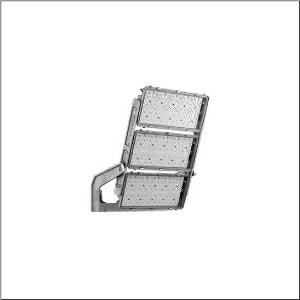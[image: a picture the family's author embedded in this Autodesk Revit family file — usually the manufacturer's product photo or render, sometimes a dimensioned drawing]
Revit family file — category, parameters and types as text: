
# Revit family: floodlight_fl_11_maxi_pro_remote___pl43_5xa779528a01aa_9860
name_source: partatom
category: Lighting Fixtures
units: mm (PartAtom-declared; Revit-internal decimal feet)

## family parameters
Cut with Voids When Loaded = No
Host = Face
Light Source = No
Part Type = Normal
Room Calculation Point = No
Round Connector Dimension = Use Diameter
Shared = No

## types (1)
- --- (1 x LED, 156040 lm, 1388 W, 5700K)
    Apparent Load = 1388 VA
    CIE Flux Codes = 25 74 99 100 100
    Color Rendering = 80
    Color Temperature = 5700K
    Default Elevation = 1800 mm
    Description = Floodlight FL 11  maxi  pro Remote floodlight; light control with lens of PMMA; cover panel of toughened safety glass, transparent; light distribution: PL43, asymmetric direct distribution, LEDcolour temperature: 5700K, colour rendering: CRI > 80, light colour: 857; brightness control: DMX+RDM; with terminal, 8-pole, max. 2.5mm², mains connection: 220..240V/380..400V AC, 50/60Hz, surge voltage resistance: line to ground: 10kV, ECG replaceable separately, LED unit replaceable without ESD environment, dustproof LED module, LED unit replaceable, LED unit replaceable on mast without ESD environment, dimming range 10..100%; floodlight with 3x LED unit of diecast aluminium, coated grey; length: 1.003mm / width: 651mm / height: 338mm; mounting bracket, of diecast aluminium, uncoated, natural, equipment: Power, protection rating (complete): IP66; insulation class (complete): insulation class I (protective earthing); certification: CE, ENEC, VDE; ball protection: ball impact resistance with accessories, only for outdoor installations, rated ambient temperature 10°C, permissible operating ambient temperature: -40..+30°C, permissible storage temperature: -40..+85°C; packaging unit: 1 piece

Light Distribution: PL43
    Height = 320 mm
    Lamp = 1 x LED
    Lamp Light Flux = 156040 lm
    Lamp Power = 1388 W
    Lamp count = 1
    Length = 1002 mm
    Luminous efficacy = 112 lm/W
    Manufacturer = Siteco
    ModVariant = No
    Model = 5XA779528A01AA
    Number of Poles = 1
    OnlyDefault = Yes
    Power Factor = 1
    Product Name = Floodlight FL 11 maxi pro Remote | PL43
    Product group = floodlight | pylon top
    ProductGroupID = 6101
    Protection Class = Protection class I
    Protection Degree = IP 66
    RLX_Detail_Level = 1
    RlxData = <blob elided: 52225 chars, md5=ae667bb4>
    Socket = socket
    Standby Power = 0 W
    System Light Flux = 156040 lm
    System Power = 1388 W
    Type Comments = factory setting: luminous flux: 100 % | dim-lin: 255 | 955 mA
    Type Image = l_1006784.jpg
    URL = http://relux.com
    VarID = @adj_001139
    Voltage = 0 V
    Weight = 0.00 kg
    Width = 655 mm

## geometry (parser evidence)
native form markers: Blend x4, Sweep x15
no freeform markers — native parametric forms only
